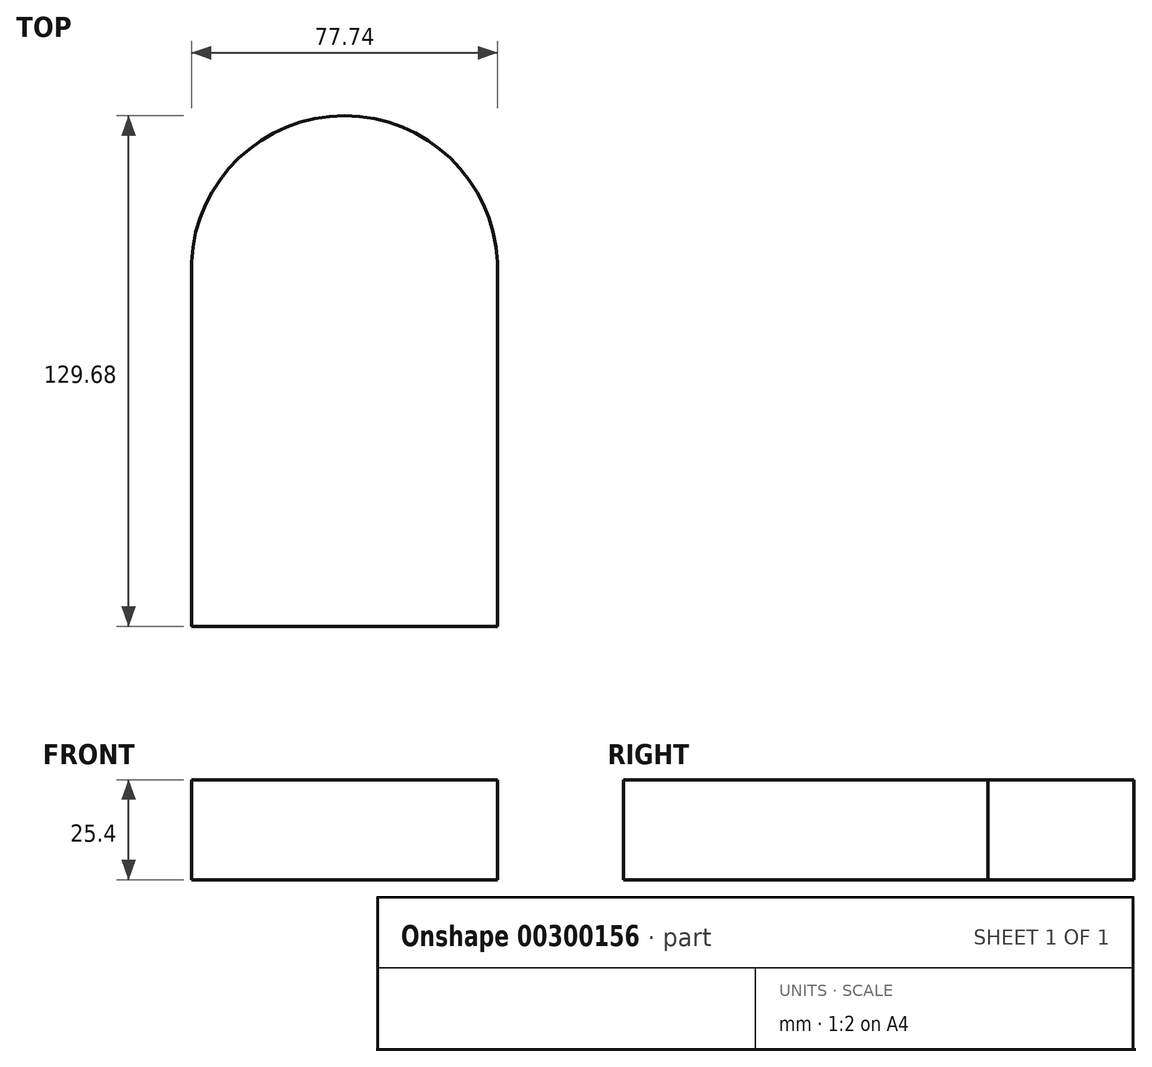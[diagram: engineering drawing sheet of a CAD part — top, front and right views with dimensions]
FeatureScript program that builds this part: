
annotation { "Feature Type Name" : "Feature", "Feature Type Description" : "" }
export const myFeature = defineFeature(function(context is Context, id is Id, definition is map)
    precondition{}
    {
        {
            var Q0;
            Q0=qCreatedBy(makeId("Top.planeOp"),FACE);
            var sketch = newSketch(context, id + "F0", { "sketchPlane" : qUnion([Q0])});
            skLineSegment(sketch, "E0.bottom", {"start": v(-38.49, 36.4) * mm, "end": v(39.25, 36.4) * mm});
            skLineSegment(sketch, "E0.top", {"start": v(-38.49, -56.12) * mm, "end": v(39.25, -56.12) * mm});
            skLineSegment(sketch, "E0.left", {"start": v(-38.49, 36.4) * mm, "end": v(-38.49, -56.12) * mm});
            skLineSegment(sketch, "E0.right", {"start": v(39.25, 36.4) * mm, "end": v(39.25, -56.12) * mm});
            skArc(sketch, "E1", {"start": v(39.25, 36.4) * mm, "mid": v(0.38, 73.56) * mm, "end": v(-38.49, 36.4) * mm});
            skSolve(sketch);
        }
        {
            var Q0;
            Q0 = qSketchRegion(id + "F0", true);
            extrude(context, id + "F1", {"entities" : qUnion([Q0]), "depth" : 25.4 * mm});
        }
        {
            var Q0;
            Q0=qCreatedBy(makeId("Top.planeOp"),FACE);
            var sketch = newSketch(context, id + "F2", { "sketchPlane" : qUnion([Q0])});
            skCircle(sketch, "E2", {"center": v(0, 0) * mm, "radius": 21.94 * mm});
            skSolve(sketch);
        }
        {
            var Q0;
            Q0=sQuery(id+"F2.wireOp",EDGE,"E2");
            extrude(context, id + "F3", {"bodyType" : ToolBodyType.SURFACE, "surfaceEntities" : qUnion([Q0]), "depth" : 25.4 * mm});
        }
        {
            var Q0;
            Q0=sQuery(id+"F2.wireOp",EDGE,"E2");
            extrude(context, id + "F4", {"bodyType" : ToolBodyType.SURFACE, "surfaceEntities" : qUnion([Q0]), "depth" : 100 * mm});
        }
    });
